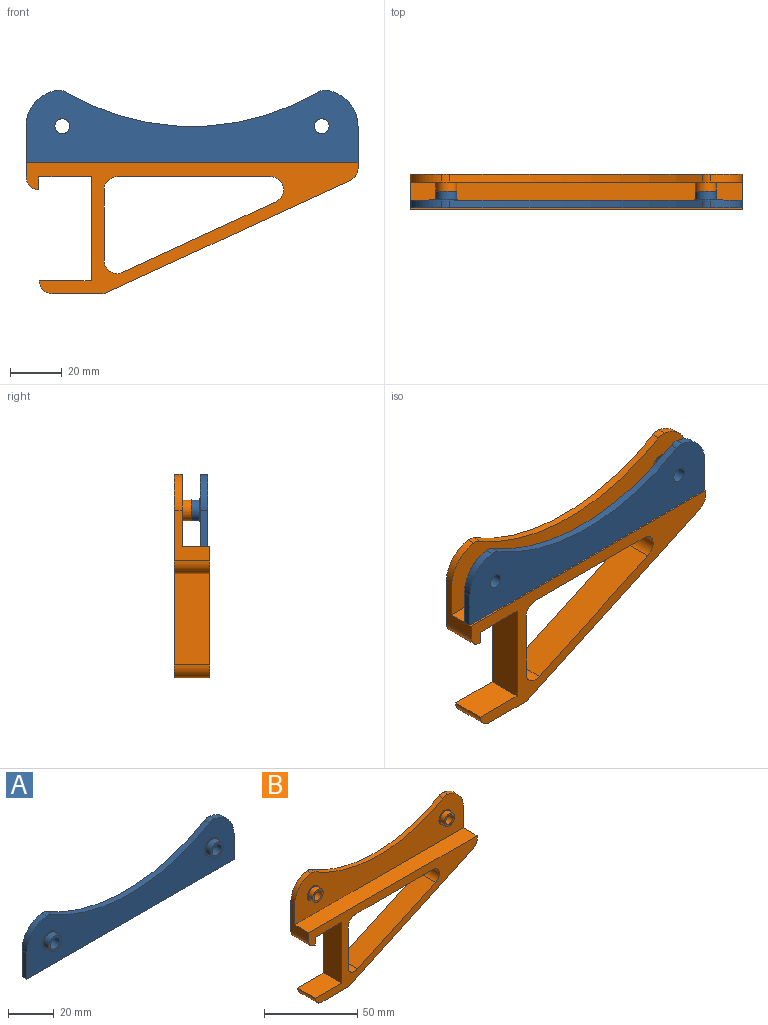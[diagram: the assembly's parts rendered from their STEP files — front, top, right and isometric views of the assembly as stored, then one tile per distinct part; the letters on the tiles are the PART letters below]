
ASSEMBLY  parts=2 mates=1
PART A: 20 faces, bbox 128x6.5x27.9 mm
  f0: cylinder r=5mm len=3.24mm, axis (0,1,0), area 10.1mm2, adj f1,f8,f10,f11
  f1: cylinder r=95.7mm len=97.4mm, axis (0,1,0), area 306.6mm2, adj f0,f2,f10,f11
  f2: cylinder r=5mm len=3.24mm, axis (0,1,0), area 10.1mm2, adj f1,f3,f10,f11
  f3: cylinder r=14mm len=13.87mm, axis (0,1,0), area 60.1mm2, adj f2,f4,f10,f11
  f4: plane 14x3mm, normal (-1,0,0), area 42mm2, adj f3,f5,f10,f11
  f5: plane 128x3mm, normal (0,0,-1), area 384mm2, adj f4,f6,f10,f11
  f6: plane 14x3mm, normal (1,0,0), area 42mm2, adj f5,f8,f10,f11
  f7: cylinder r=2.88mm len=6.45mm, axis (0,1,0), area 116.5mm2, adj f11,f17
  f8: cylinder r=14mm len=13.87mm, axis (0,1,0), area 60.1mm2, adj f0,f6,f10,f11
  f9: cylinder r=2.88mm len=6.45mm, axis (0,1,0), area 116.5mm2, adj f11,f19
  f10: plane 128x27.91mm, normal (0,-1,0), area 2417.3mm2, adj f0,f1,f2,f3,f4,f5,f6,f8
  f11: plane 128x27.91mm, normal (0,1,0), area 2492.6mm2, adj f0,f1,f2,f3,f4,f5,f6,f7
  f12: cylinder r=4.5mm len=9mm, axis (0,1,0), area 7.1mm2, adj f10,f13
  f13: plane 9x9mm, normal (0,-1,0), area 12.7mm2, adj f12,f16
  f14: cylinder r=4.5mm len=9mm, axis (0,1,0), area 7.1mm2, adj f10,f15
  f15: plane 9x9mm, normal (0,-1,0), area 12.7mm2, adj f14,f18
  f16: cylinder r=4.03mm len=8.05mm, axis (0,1,0), area 80.9mm2, adj f13,f17
  f17: plane 8.05x8.05mm, normal (0,-1,0), area 24.9mm2, adj f7,f16
  f18: cylinder r=4.03mm len=8.05mm, axis (0,1,0), area 80.9mm2, adj f15,f19
  f19: plane 8.05x8.05mm, normal (0,-1,0), area 24.9mm2, adj f9,f18
PART B: 37 faces, bbox 128x13.5x78.5 mm
  f0: plane 59.24x13.5mm, normal (0,0,-1), area 799.8mm2, adj f19,f29,f34,f36
  f1: plane 59.24x27.29mm, normal (-0.42,0,0.91), area 880.6mm2, adj f19,f29,f34,f35
  f2: cylinder r=95.7mm len=97.4mm, axis (0,1,0), area 306.6mm2, adj f3,f16,f18,f19
  f3: cylinder r=5mm len=3.24mm, axis (0,1,0), area 10.1mm2, adj f2,f4,f18,f19
  f4: cylinder r=14mm len=13.87mm, axis (0,1,0), area 60.1mm2, adj f3,f5,f18,f19
  f5: plane 19.5x13.5mm, normal (-1,0,0), area 116.2mm2, adj f4,f18,f19,f28,f29,f30
  f6: plane 13.5x5mm, normal (1,0,0), area 67.5mm2, adj f7,f19,f29,f30
  f7: plane 20.1x13.5mm, normal (0,0,-1), area 271.3mm2, adj f6,f8,f19,f29
  f8: plane 40.1x13.5mm, normal (-1,0,0), area 541.3mm2, adj f7,f9,f19,f29
  f9: plane 20x13.5mm, normal (0,0,1), area 270mm2, adj f8,f19,f29,f31
  f10: plane 18.9x13.5mm, normal (0,0,-1), area 255.2mm2, adj f19,f29,f31,f32
  f11: plane 94x43.3mm, normal (0.42,0,-0.91), area 1397.1mm2, adj f19,f29,f32,f33
  f12: plane 16.3x13.5mm, normal (1,0,0), area 73mm2, adj f13,f18,f19,f28,f29,f33
  f13: cylinder r=14mm len=13.87mm, axis (0,1,0), area 60.1mm2, adj f12,f16,f18,f19
  f14: plane 27.29x13.5mm, normal (1,0,0), area 368.4mm2, adj f19,f29,f35,f36
  f15: cylinder r=2.88mm len=6.45mm, axis (0,1,0), area 116.5mm2, adj f19,f21
  f16: cylinder r=5mm len=3.24mm, axis (0,1,0), area 10.1mm2, adj f2,f13,f18,f19
  f17: cylinder r=2.88mm len=6.45mm, axis (0,1,0), area 116.5mm2, adj f19,f23
  f18: plane 128x27.91mm, normal (0,-1,0), area 2417.3mm2, adj f2,f3,f4,f5,f12,f13,f16,f24
  f19: plane 128x78.51mm, normal (0,1,0), area 4096.4mm2, adj f0,f1,f2,f3,f4,f5,f6,f7
  f20: cylinder r=4.03mm len=8.05mm, axis (0,1,0), area 80.9mm2, adj f21,f25
  f21: plane 8.05x8.05mm, normal (0,-1,0), area 24.9mm2, adj f15,f20
  f22: cylinder r=4.03mm len=8.05mm, axis (0,1,0), area 80.9mm2, adj f23,f27
  f23: plane 8.05x8.05mm, normal (0,-1,0), area 24.9mm2, adj f17,f22
  f24: cylinder r=4.5mm len=9mm, axis (0,1,0), area 7.1mm2, adj f18,f25
  f25: plane 9x9mm, normal (0,-1,0), area 12.7mm2, adj f20,f24
  f26: cylinder r=4.5mm len=9mm, axis (0,1,0), area 7.1mm2, adj f18,f27
  f27: plane 9x9mm, normal (0,-1,0), area 12.7mm2, adj f22,f26
  f28: plane 128x10.5mm, normal (0,0,1), area 1344mm2, adj f5,f12,f18,f29
  f29: plane 128x50.6mm, normal (0,-1,0), area 1603.8mm2, adj f0,f1,f5,f6,f7,f8,f9,f10
  f30: cylinder r=5mm len=13.5mm, axis (0,1,0), area 106mm2, adj f5,f6,f19,f29
  f31: cylinder r=5mm len=13.5mm, axis (0,1,0), area 106mm2, adj f9,f10,f19,f29
  f32: cylinder r=5mm len=13.5mm, axis (0,1,0), area 29.1mm2, adj f10,f11,f19,f29
  f33: cylinder r=5mm len=13.5mm, axis (0,-1,0), area 76.9mm2, adj f11,f12,f19,f29
  f34: cylinder r=5mm len=13.5mm, axis (0,-1,0), area 182.9mm2, adj f0,f1,f19,f29
  f35: cylinder r=5mm len=13.5mm, axis (0,1,0), area 135.2mm2, adj f1,f14,f19,f29
  f36: cylinder r=5mm len=13.5mm, axis (0,1,0), area 106mm2, adj f0,f14,f19,f29
PLACE A rot(axis=(0,0,1),180deg) t=(33.06,-14.83,39.97)mm
PLACE B t=(-30.94,-1.93,8.72)mm fixed
MATE fastened A.f8 <-> B.f4  axis (0,1,0) through (-80.94,-8.38,53.97)mm
